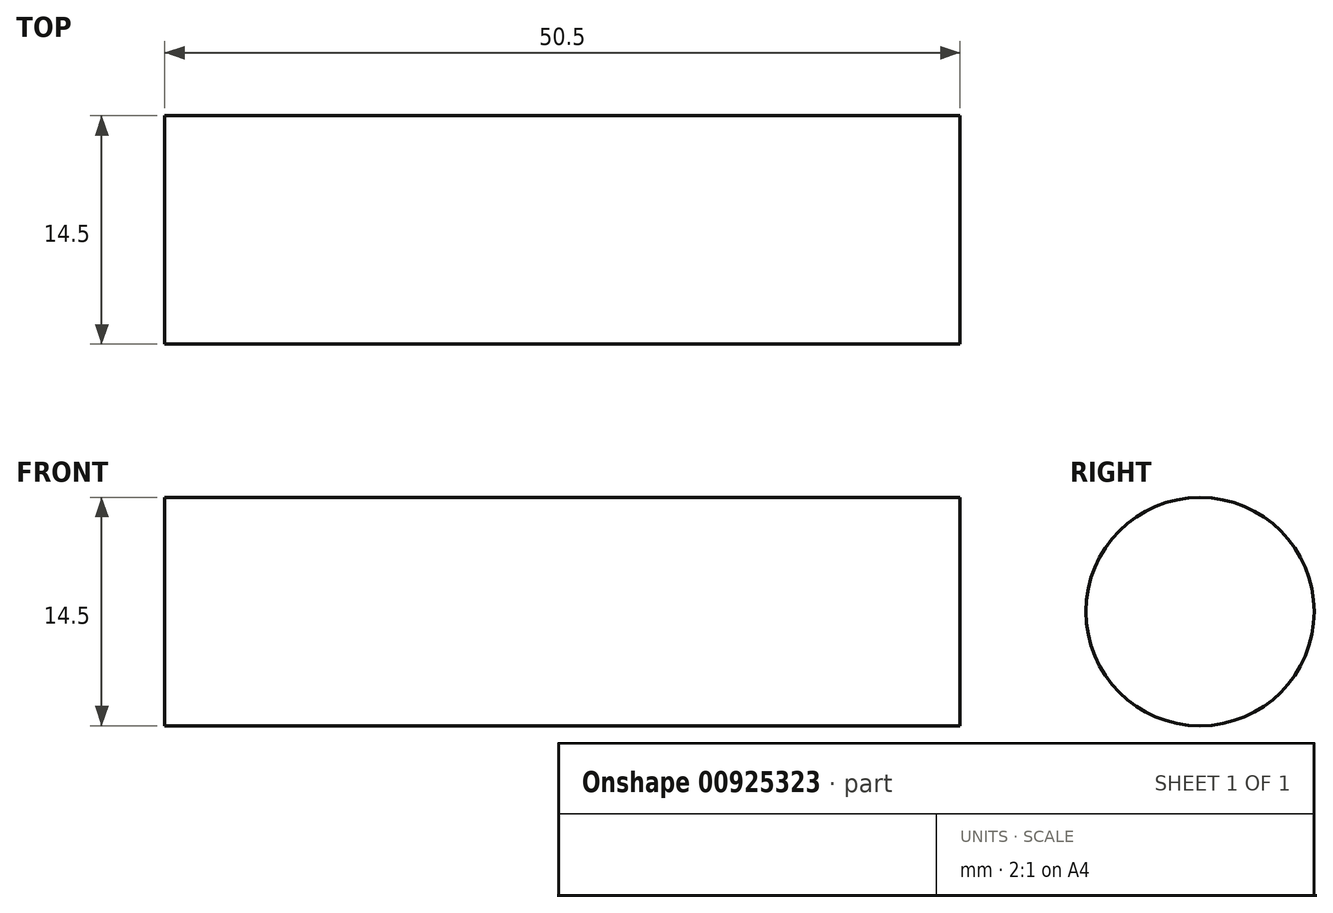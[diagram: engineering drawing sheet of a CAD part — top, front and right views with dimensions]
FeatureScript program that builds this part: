
annotation { "Feature Type Name" : "Feature", "Feature Type Description" : "" }
export const myFeature = defineFeature(function(context is Context, id is Id, definition is map)
    precondition{}
    {
        {
            var Q0;
            Q0=qCreatedBy(makeId("Top.planeOp"),FACE);
            var sketch = newSketch(context, id + "F0", { "sketchPlane" : qUnion([Q0])});
            skLineSegment(sketch, "E0", {"start": v(0, 0) * mm, "end": v(25, 0) * mm, "construction": true});
            skArc(sketch, "E1", {"start": v(25, -20) * mm, "mid": v(39.14, -14.14) * mm, "end": v(45, 0) * mm});
            skLineSegment(sketch, "E2", {"start": v(25, -20) * mm, "end": v(0, -20) * mm});
            skLineSegment(sketch, "E3", {"start": v(0, 0) * mm, "end": v(0, 34.01) * mm, "construction": true});
            skCircle(sketch, "E4", {"center": v(25, 0) * mm, "radius": 10 * mm, "construction": true});
            skLineSegment(sketch, "E5", {"start": v(25, 0) * mm, "end": v(35, 0) * mm, "construction": true});
            skSolve(sketch);
        }
        {
            var Q0;
            Q0=qCreatedBy(makeId("Front.planeOp"),FACE);
            var sketch = newSketch(context, id + "F1", { "sketchPlane" : qUnion([Q0])});
            skLineSegment(sketch, "E6", {"start": v(0, 16) * mm, "end": v(35, 16) * mm, "construction": true});
            skLineSegment(sketch, "E7", {"start": v(35, 0) * mm, "end": v(35, 16) * mm, "construction": true});
            skLineSegment(sketch, "E8", {"start": v(0, 0) * mm, "end": v(0, 16) * mm, "construction": true});
            skArc(sketch, "E9", {"start": v(45, 0) * mm, "mid": v(42.07, 9.3) * mm, "end": v(35, 16) * mm});
            skLineSegment(sketch, "E10", {"start": v(45, 0) * mm, "end": v(45, -5.37) * mm, "construction": true});
            skLineSegment(sketch, "E11", {"start": v(45, 0) * mm, "end": v(45.25, -4.77) * mm, "construction": true});
            skLineSegment(sketch, "E12", {"start": v(35, 16) * mm, "end": v(34.95, 15) * mm});
            skLineSegment(sketch, "E13", {"start": v(34.95, 15) * mm, "end": v(0, 15) * mm, "construction": true});
            skLineSegment(sketch, "E14", {"start": v(45, -1) * mm, "end": v(0, -1) * mm, "construction": true});
            skArc(sketch, "E15", {"start": v(39.73, -6) * mm, "mid": v(43.36, -4.55) * mm, "end": v(45, -1) * mm});
            skLineSegment(sketch, "E16", {"start": v(45, -1) * mm, "end": v(45, 2.28) * mm, "construction": true});
            skLineSegment(sketch, "E17", {"start": v(45, -1) * mm, "end": v(45.17, 2.22) * mm, "construction": true});
            skLineSegment(sketch, "E18", {"start": v(39.73, -6) * mm, "end": v(0, -6) * mm, "construction": true});
            skSolve(sketch);
        }
        {
            var Q0;
            Q0=sQuery(id+"F1.wireOp",VERTEX,"E14.start");
            var Q1;
            Q1=qCreatedBy(makeId("Top.planeOp"),FACE);
            cPlane(context, id + "F2", {"entities" : qUnion([Q0, Q1]), "cplaneType" : CPlaneType.PLANE_POINT, "offset" : 25 * mm, "width" : 150 * mm, "height" : 150 * mm});
        }
        {
            var Q0;
            Q0=sQuery(id+"F1.wireOp",VERTEX,"E6.start");
            var Q1;
            Q1=qCreatedBy(makeId("Top.planeOp"),FACE);
            cPlane(context, id + "F3", {"entities" : qUnion([Q0, Q1]), "cplaneType" : CPlaneType.PLANE_POINT, "offset" : 25 * mm, "width" : 150 * mm, "height" : 150 * mm});
        }
        {
            var Q0;
            Q0=qCreatedBy(makeId("Right.planeOp"),FACE);
            var sketch = newSketch(context, id + "F4", { "sketchPlane" : qUnion([Q0])});
            skCircle(sketch, "E19", {"center": v(-5, 3) * mm, "radius": 7.25 * mm});
            skSolve(sketch);
        }
        {
            var Q0;
            Q0=makeQuery(id+"F4.imprint","IMPRINT",FACE,{"disambiguationData":[TD([[makeQuery(id+"F4.imprint","IMPRINT",EDGE,{"derivedFrom":sQuery(id+"F4.wireOp",EDGE,"E19")}),1.0]])]});
            extrude(context, id + "F5", {"entities" : qUnion([Q0]), "endBound" : BoundingType.SYMMETRIC, "depth" : 50.5 * mm, "offsetDistance" : 25 * mm, "hasSecondDirection" : true, "secondDirectionOppositeDirection" : true, "secondDirectionDepth" : 25 * mm});
        }
    });
